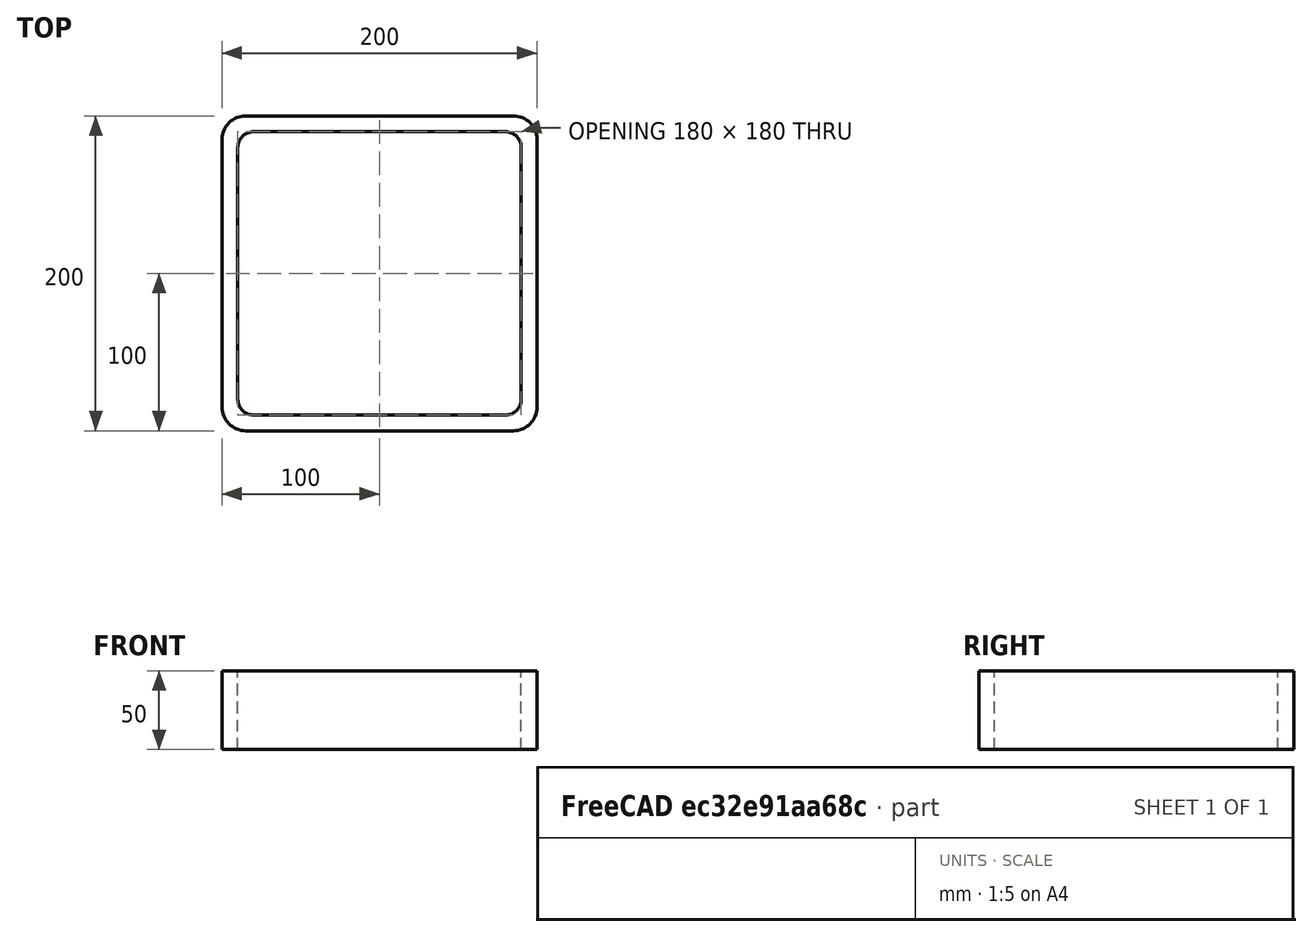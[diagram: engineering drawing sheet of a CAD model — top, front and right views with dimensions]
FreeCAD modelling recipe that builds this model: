
FCSTD DOCUMENT  (FreeCAD 0.15R4671 (Git))
Label: Square hollow section 200x200x10 EN10219 S235JRH
License: All rights reserved
LicenseURL: http://en.wikipedia.org/wiki/All_rights_reserved
objects: Sketcher::SketchObject×1, Part::Extrusion×1
note: 2 computed .brp shape members not serialized (recipe doc carries the construction recipe); baked Part::Feature solids carry a one-line shape summary decoded from their .brp

FEATURE [Sketcher::SketchObject] Sketch
  sketch-geometry (16):
    g0: LineSegment StartX=-80 StartY=90 StartZ=0 EndX=80 EndY=90 EndZ=0
    g1: LineSegment StartX=90 StartY=80 StartZ=0 EndX=90 EndY=-80 EndZ=0
    g2: LineSegment StartX=80 StartY=-90 StartZ=0 EndX=-80 EndY=-90 EndZ=0
    g3: LineSegment StartX=-90 StartY=-80 StartZ=0 EndX=-90 EndY=80 EndZ=0
    g4: LineSegment StartX=-85 StartY=100 StartZ=0 EndX=85 EndY=100 EndZ=0
    g5: LineSegment StartX=100 StartY=85 StartZ=0 EndX=100 EndY=-85 EndZ=0
    g6: LineSegment StartX=85 StartY=-100 StartZ=0 EndX=-85 EndY=-100 EndZ=0
    g7: LineSegment StartX=-100 StartY=-85 StartZ=0 EndX=-100 EndY=85 EndZ=0
    g8: ArcOfCircle CenterX=-80 CenterY=80 CenterZ=0 NormalX=0 NormalY=0 NormalZ=1 Radius=10 StartAngle=1.5708 EndAngle=3.14159
    g9: ArcOfCircle CenterX=80 CenterY=80 CenterZ=0 NormalX=0 NormalY=0 NormalZ=1 Radius=10 StartAngle=0 EndAngle=1.5708
    g10: ArcOfCircle CenterX=80 CenterY=-80 CenterZ=0 NormalX=0 NormalY=0 NormalZ=1 Radius=10 StartAngle=4.71239 EndAngle=6.28319
    g11: ArcOfCircle CenterX=-80 CenterY=-80 CenterZ=0 NormalX=0 NormalY=0 NormalZ=1 Radius=10 StartAngle=3.14159 EndAngle=4.71239
    g12: ArcOfCircle CenterX=85 CenterY=85 CenterZ=0 NormalX=0 NormalY=0 NormalZ=1 Radius=15 StartAngle=0 EndAngle=1.5708
    g13: ArcOfCircle CenterX=85 CenterY=-85 CenterZ=0 NormalX=0 NormalY=0 NormalZ=1 Radius=15 StartAngle=4.71239 EndAngle=6.28319
    g14: ArcOfCircle CenterX=-85 CenterY=-85 CenterZ=0 NormalX=0 NormalY=0 NormalZ=1 Radius=15 StartAngle=3.14159 EndAngle=4.71239
    g15: ArcOfCircle CenterX=-85 CenterY=85 CenterZ=0 NormalX=0 NormalY=0 NormalZ=1 Radius=15 StartAngle=1.5708 EndAngle=3.14159
  constraints (36):
    c: Horizontal(g2)
    c: Vertical(g3)
    c: Horizontal(g6)
    c: Vertical(g7)
    c: Tangent(g3,g8) = 1.5708
    c: Tangent(g0,g8) = 1.5708
    c: Tangent(g0,g9) = 1.5708
    c: Tangent(g1,g9) = 1.5708
    c: Tangent(g1,g10) = 1.5708
    c: Tangent(g2,g10) = 1.5708
    c: Tangent(g2,g11) = 1.5708
    c: Tangent(g3,g11) = 1.5708
    c: Tangent(g4,g12) = 1.5708
    c: Tangent(g5,g12) = 1.5708
    c: Tangent(g5,g13) = 1.5708
    c: Tangent(g6,g13) = 1.5708
    c: Tangent(g6,g14) = 1.5708
    c: Tangent(g7,g14) = 1.5708
    c: Tangent(g7,g15) = 1.5708
    c: Tangent(g4,g15) = 1.5708
    c: Equal(g9,g8)
    c: Equal(g9,g11)
    c: Equal(g9,g10)
    c: Equal(g12,g15)
    c: Equal(g12,g14)
    c: Equal(g12,g13)
    c: Symmetric(g4,g6,g-1)
    c: Symmetric(g7,g5,g-2)
    c: DistanceY(g4,g6) = -200
    c: DistanceX(g7,g5) = 200
    c: Symmetric(g3,g1,g-2)
    c: Symmetric(g0,g2,g-1)
    c: DistanceY(g0,g4) = 10
    c: DistanceX(g5,g1) = -10
    c: Radius(g9) = 10
    c: Radius(g12) = 15
FEATURE [Part::Extrusion] Extrude  label="Square hollow section 200x200x10 EN10219 S235JRH"
  Base = -> Sketch
  Dir = (0,0,50)
  Solid = true
